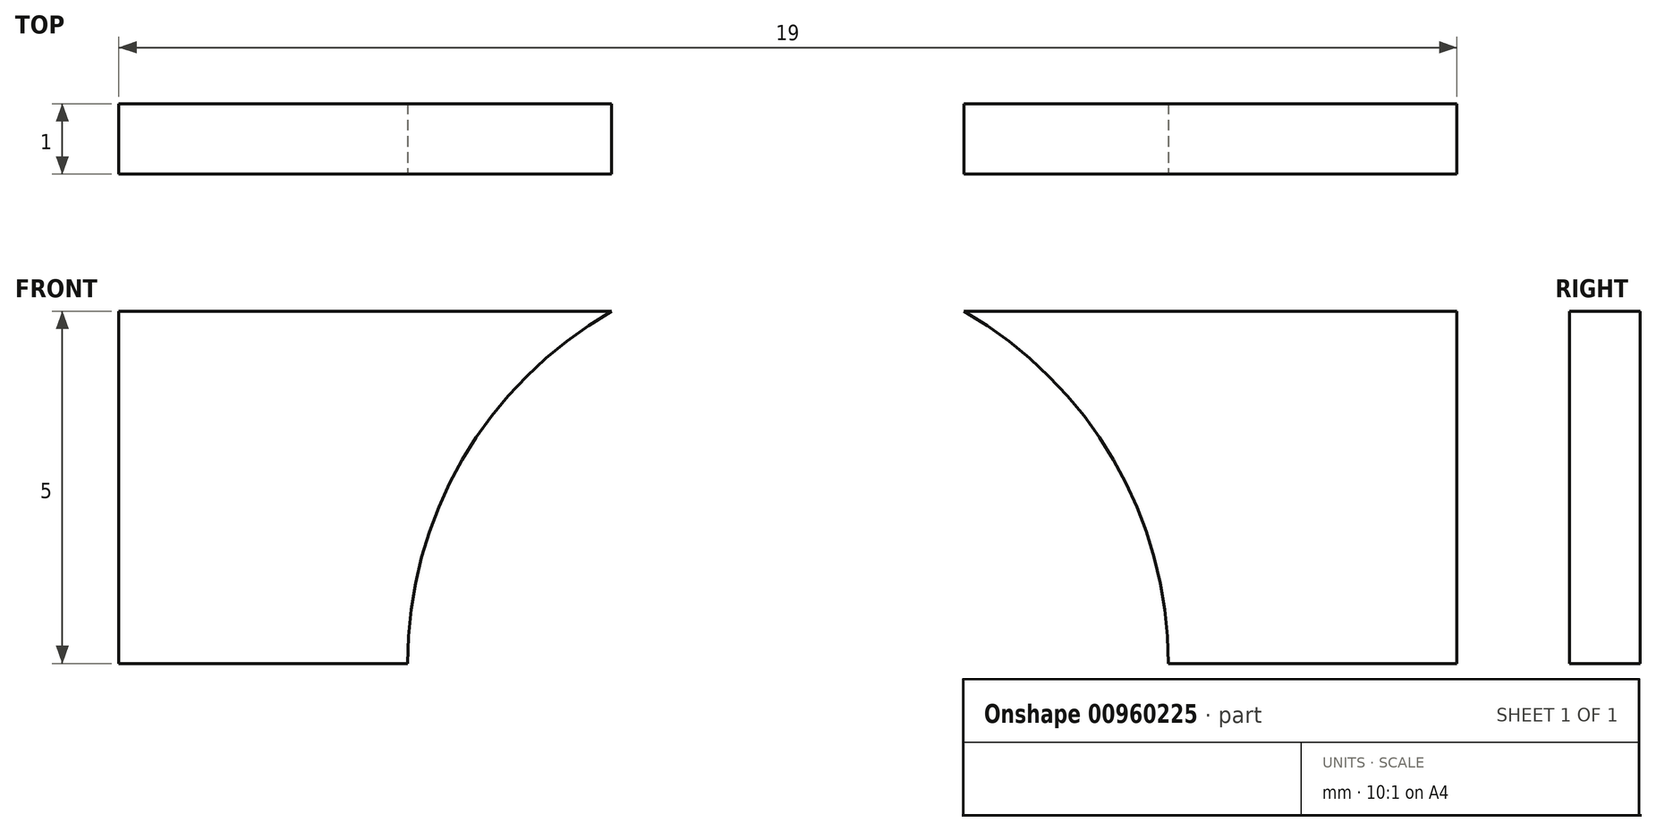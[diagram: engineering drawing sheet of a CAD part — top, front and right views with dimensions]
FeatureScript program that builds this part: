
annotation { "Feature Type Name" : "Feature", "Feature Type Description" : "" }
export const myFeature = defineFeature(function(context is Context, id is Id, definition is map)
    precondition{}
    {
        {
            var Q0;
            Q0=qCreatedBy(makeId("Front.planeOp"),FACE);
            var sketch = newSketch(context, id + "F0", { "sketchPlane" : qUnion([Q0])});
            skLineSegment(sketch, "E0.bottom", {"start": v(-9.5, 0) * mm, "end": v(-5.5, 0) * mm});
            skLineSegment(sketch, "E0.top", {"start": v(-9.5, -5) * mm, "end": v(-5.4, -5) * mm});
            skLineSegment(sketch, "E0.left", {"start": v(-9.5, 0) * mm, "end": v(-9.5, -5) * mm});
            skArc(sketch, "E1", {"start": v(-2.5, 0) * mm, "mid": v(-4.62, -2.1) * mm, "end": v(-5.4, -5) * mm});
            skLineSegment(sketch, "E2", {"start": v(-2.5, 0) * mm, "end": v(-5.5, 0) * mm});
            skLineSegment(sketch, "E3.MirrorCS", {"start": v(9.5, -5) * mm, "end": v(5.4, -5) * mm});
            skLineSegment(sketch, "E4.MirrorCS", {"start": v(9.5, 0) * mm, "end": v(5.5, 0) * mm});
            skLineSegment(sketch, "E5.MirrorCS", {"start": v(9.5, 0) * mm, "end": v(9.5, -5) * mm});
            skLineSegment(sketch, "E6.MirrorCS", {"start": v(2.5, 0) * mm, "end": v(5.5, 0) * mm});
            skArc(sketch, "E7.MirrorCS", {"start": v(2.5, 0) * mm, "mid": v(4.62, -2.1) * mm, "end": v(5.4, -5) * mm});
            skSolve(sketch);
        }
        {
            var Q0;
            Q0 = qSketchRegion(id + "F0", true);
            extrude(context, id + "F1", {"entities" : qUnion([Q0]), "oppositeDirection" : true, "depth" : 1 * mm, "offsetDistance" : 25 * mm});
        }
    });
